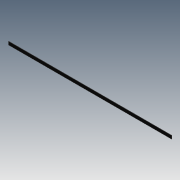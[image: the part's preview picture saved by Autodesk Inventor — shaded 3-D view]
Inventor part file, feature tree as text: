
AUTODESK INVENTOR PART (.ipt)
format: ipt  version: 2012 (Build 160160000, 160)  size: 65,024 bytes
history: native  units: in
note: dims shown in document units (in); Inventor stores cm internally (conversion verified against a paired STEP export)
features: extrude x1, sketch x1
ambient origin geometry x8: Origin, YZ Plane, XZ Plane, XY Plane, X Axis, Y Axis, Z Axis, Center Point
bodies: Solid1 (feature_tree)
feature tree (2):
  extrude  "Extrusion1"  Depth=1.0in
  sketch  "Sketch1"  dims[d0=50.25in d1=1.0in d2=0.0625in d3=0.0in]
